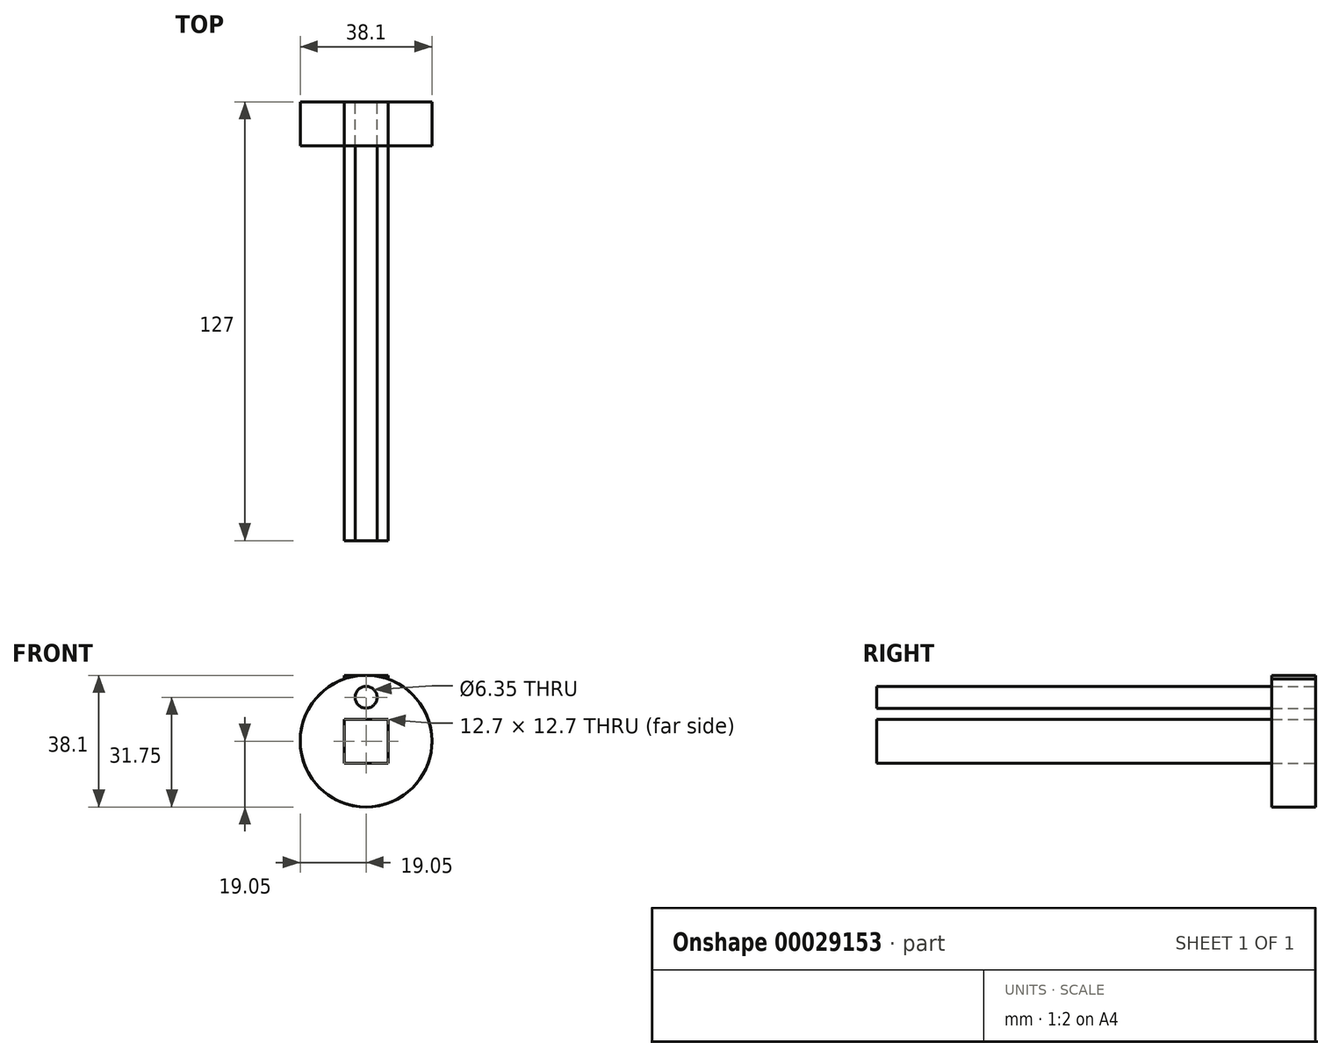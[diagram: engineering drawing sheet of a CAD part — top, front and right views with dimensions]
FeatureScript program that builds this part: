
annotation { "Feature Type Name" : "Feature", "Feature Type Description" : "" }
export const myFeature = defineFeature(function(context is Context, id is Id, definition is map)
    precondition{}
    {
        {
            var Q0;
            Q0=qCreatedBy(makeId("Front.planeOp"),FACE);
            var sketch = newSketch(context, id + "F0", { "sketchPlane" : qUnion([Q0])});
            skLineSegment(sketch, "E0.rect.bottom", {"start": v(6.35, 6.35) * mm, "end": v(-6.35, 6.35) * mm});
            skLineSegment(sketch, "E0.rect.top", {"start": v(6.35, -6.35) * mm, "end": v(-6.35, -6.35) * mm});
            skLineSegment(sketch, "E0.rect.left", {"start": v(6.35, 6.35) * mm, "end": v(6.35, -6.35) * mm});
            skLineSegment(sketch, "E0.rect.right", {"start": v(-6.35, 6.35) * mm, "end": v(-6.35, -6.35) * mm});
            skPoint(sketch, "E0.rect.middle", {"position": v(0, 0) * mm});
            skLineSegment(sketch, "E1.MirrorCS", {"start": v(-6.35, 6.35) * mm, "end": v(-6.35, 19.05) * mm});
            skLineSegment(sketch, "E2.MirrorCS", {"start": v(6.35, 6.35) * mm, "end": v(6.35, 19.05) * mm});
            skLineSegment(sketch, "E3.MirrorCS", {"start": v(6.35, 19.05) * mm, "end": v(-6.35, 19.05) * mm});
            skPoint(sketch, "E4.MirrorP", {"position": v(0, 12.7) * mm});
            skCircle(sketch, "E5", {"center": v(0, 12.7) * mm, "radius": 3.18 * mm});
            skCircle(sketch, "E6", {"center": v(0, 0) * mm, "radius": 19.05 * mm});
            skSolve(sketch);
        }
        {
            var Q0;
            Q0=makeQuery(id+"F0.imprint","IMPRINT",FACE,{"disambiguationData":[TD([[makeQuery(id+"F0.imprint","IMPRINT",EDGE,{"derivedFrom":sQuery(id+"F0.wireOp",EDGE,"E0.rect.bottom")}),1.0]])]});
            extrude(context, id + "F1", {"entities" : qUnion([Q0]), "depth" : 127 * mm});
        }
        {
            var Q0;
            {var subQ1=sQuery(id+"F0.wireOp",EDGE,"E3.MirrorCS");var subQ3=sQuery(id+"F0.wireOp",EDGE,"E2.MirrorCS");var subQ5=makeQuery(id+"F0.imprint","INTERSECT",VERTEX,{"derivedFrom":[subQ3,subQ1]});Q0=makeQuery(id+"F0.imprint","IMPRINT",FACE,{"disambiguationData":[TD([[makeQuery(id+"F0.imprint","IMPRINT",EDGE,{"disambiguationData":[TD([[subQ5,1.0]])],"derivedFrom":subQ3}),1.0]])]});}
            var Q1;
            {var subQ1=sQuery(id+"F0.wireOp",EDGE,"E3.MirrorCS");var subQ3=sQuery(id+"F0.wireOp",EDGE,"E1.MirrorCS");var subQ5=makeQuery(id+"F0.imprint","INTERSECT",VERTEX,{"derivedFrom":[subQ3,subQ1]});Q1=makeQuery(id+"F0.imprint","IMPRINT",FACE,{"disambiguationData":[TD([[makeQuery(id+"F0.imprint","IMPRINT",EDGE,{"disambiguationData":[TD([[subQ5,1.0]])],"derivedFrom":subQ3}),-1.0]])]});}
            var Q2;
            {var subQ6=sQuery(id+"F0.wireOp",EDGE,"E0.rect.bottom");Q2=makeQuery(id+"F0.imprint","IMPRINT",FACE,{"disambiguationData":[TD([[makeQuery(id+"F0.imprint","IMPRINT",EDGE,{"derivedFrom":subQ6}),-1.0]])]});}
            extrude(context, id + "F2", {"entities" : qUnion([Q0, Q1, Q2]), "operationType" : NewBodyOperationType.ADD, "depth" : 12.7 * mm});
        }
        {
            var Q0;
            Q0=makeQuery(id+"F0.imprint","IMPRINT",FACE,{"disambiguationData":[TD([[makeQuery(id+"F0.imprint","IMPRINT",EDGE,{"derivedFrom":sQuery(id+"F0.wireOp",EDGE,"E0.rect.top")}),1.0]])]});
            var Q1;
            {var subQ6=sQuery(id+"F0.wireOp",EDGE,"E0.rect.bottom");Q1=makeQuery(id+"F0.imprint","IMPRINT",FACE,{"disambiguationData":[TD([[makeQuery(id+"F0.imprint","IMPRINT",EDGE,{"derivedFrom":subQ6}),-1.0]])]});}
            var Q2;
            Q2=sQuery(id+"F0.wireOp",EDGE,"E6");
            extrude(context, id + "F3", {"entities" : qUnion([Q0, Q1]), "surfaceEntities" : qUnion([Q2]), "depth" : 12.7 * mm});
        }
        {
            var Q0;
            Q0=makeQuery(id+"F0.imprint","IMPRINT",FACE,{"disambiguationData":[TD([[makeQuery(id+"F0.imprint","IMPRINT",EDGE,{"derivedFrom":sQuery(id+"F0.wireOp",EDGE,"E5")}),1.0]])]});
            extrude(context, id + "F4", {"entities" : qUnion([Q0]), "depth" : 127 * mm});
        }
    });
